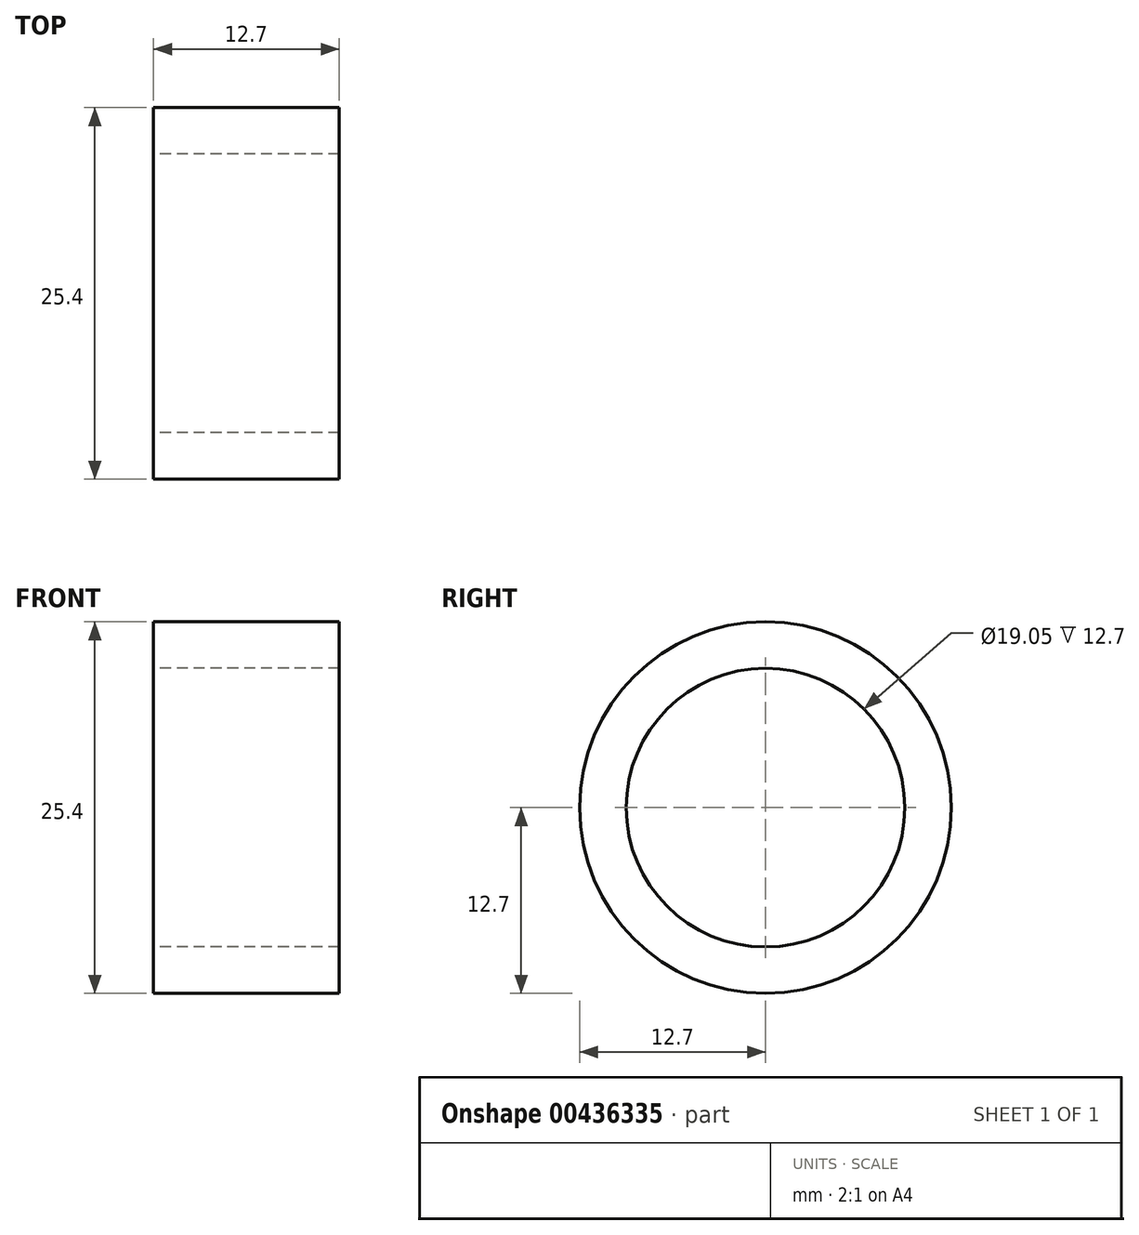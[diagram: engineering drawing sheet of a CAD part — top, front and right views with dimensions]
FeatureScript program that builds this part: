
annotation { "Feature Type Name" : "Feature", "Feature Type Description" : "" }
export const myFeature = defineFeature(function(context is Context, id is Id, definition is map)
    precondition{}
    {
        {
            var Q0;
            Q0=qCreatedBy(makeId("Right.planeOp"),FACE);
            var sketch = newSketch(context, id + "F0", { "sketchPlane" : qUnion([Q0])});
            skCircle(sketch, "E0", {"center": v(0, 0) * mm, "radius": 12.7 * mm});
            skCircle(sketch, "E1", {"center": v(0, 0) * mm, "radius": 9.53 * mm});
            skSolve(sketch);
        }
        {
            var Q0;
            Q0 = qSketchRegion(id + "F0", true);
            extrude(context, id + "F1", {"entities" : qUnion([Q0]), "depth" : 12.7 * mm});
        }
    });
